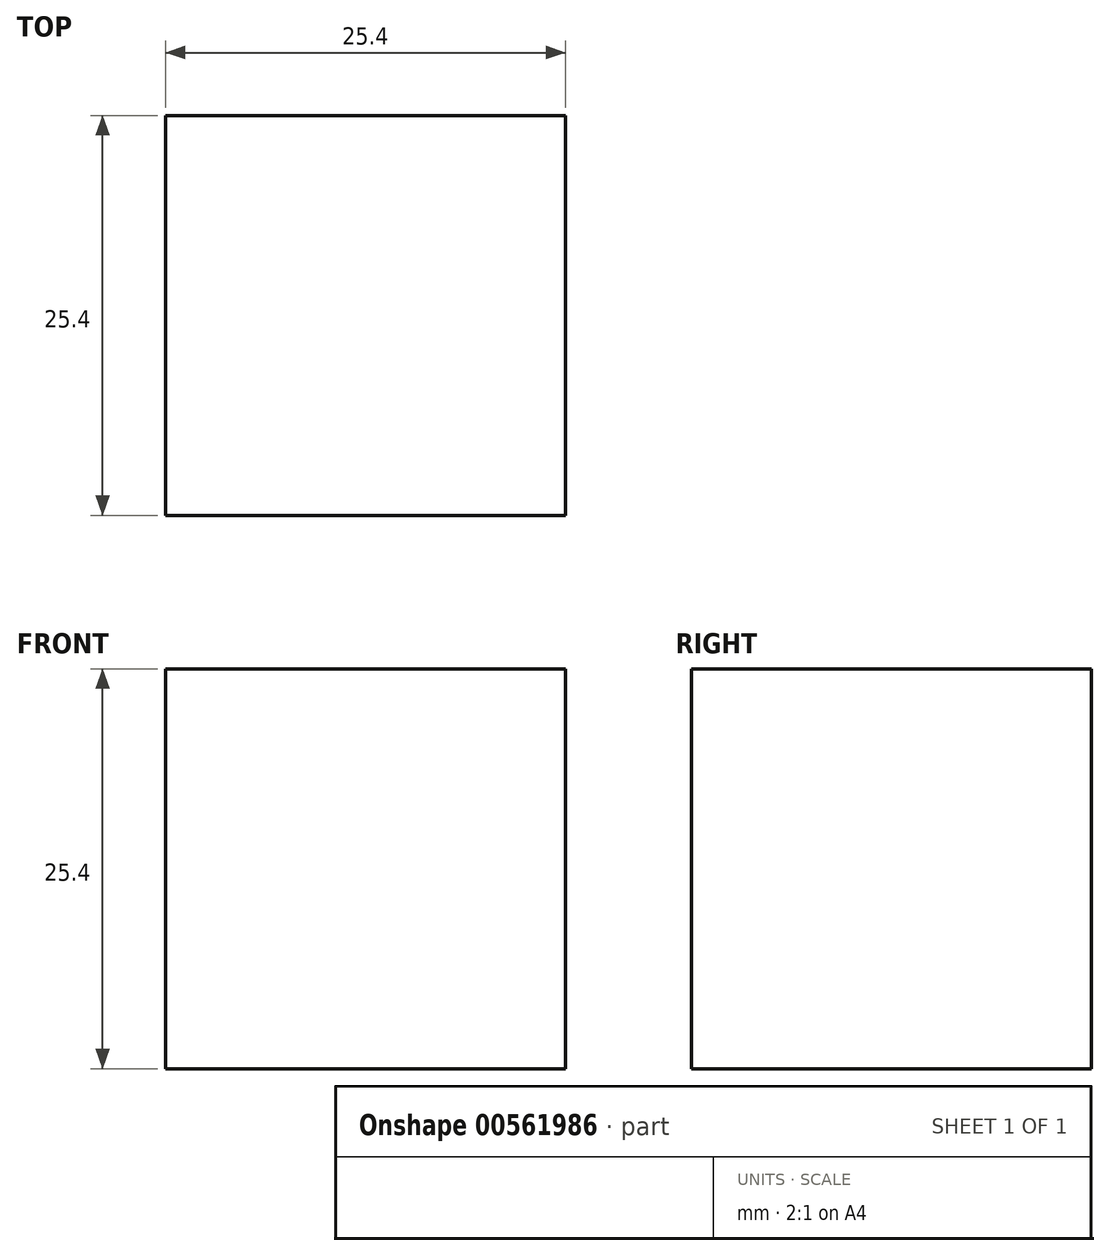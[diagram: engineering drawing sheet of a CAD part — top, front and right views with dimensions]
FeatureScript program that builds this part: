
annotation { "Feature Type Name" : "Feature", "Feature Type Description" : "" }
export const myFeature = defineFeature(function(context is Context, id is Id, definition is map)
    precondition{}
    {
        {
            var Q0;
            Q0=qCreatedBy(makeId("Front.planeOp"),FACE);
            var sketch = newSketch(context, id + "F0", { "sketchPlane" : qUnion([Q0])});
            skLineSegment(sketch, "E0.bottom", {"start": v(-13.43, 3.08) * mm, "end": v(11.97, 3.08) * mm});
            skLineSegment(sketch, "E0.top", {"start": v(-13.43, -22.32) * mm, "end": v(11.97, -22.32) * mm});
            skLineSegment(sketch, "E0.left", {"start": v(-13.43, 3.08) * mm, "end": v(-13.43, -22.32) * mm});
            skLineSegment(sketch, "E0.right", {"start": v(11.97, 3.08) * mm, "end": v(11.97, -22.32) * mm});
            skSolve(sketch);
        }
        {
            var Q0;
            Q0=makeQuery(id+"F0.imprint","IMPRINT",FACE,{"disambiguationData":[TD([[makeQuery(id+"F0.imprint","IMPRINT",EDGE,{"derivedFrom":sQuery(id+"F0.wireOp",EDGE,"E0.bottom")}),-1.0]])]});
            extrude(context, id + "F1", {"entities" : qUnion([Q0]), "depth" : 25.4 * mm, "offsetDistance" : 25.4 * mm});
        }
    });
